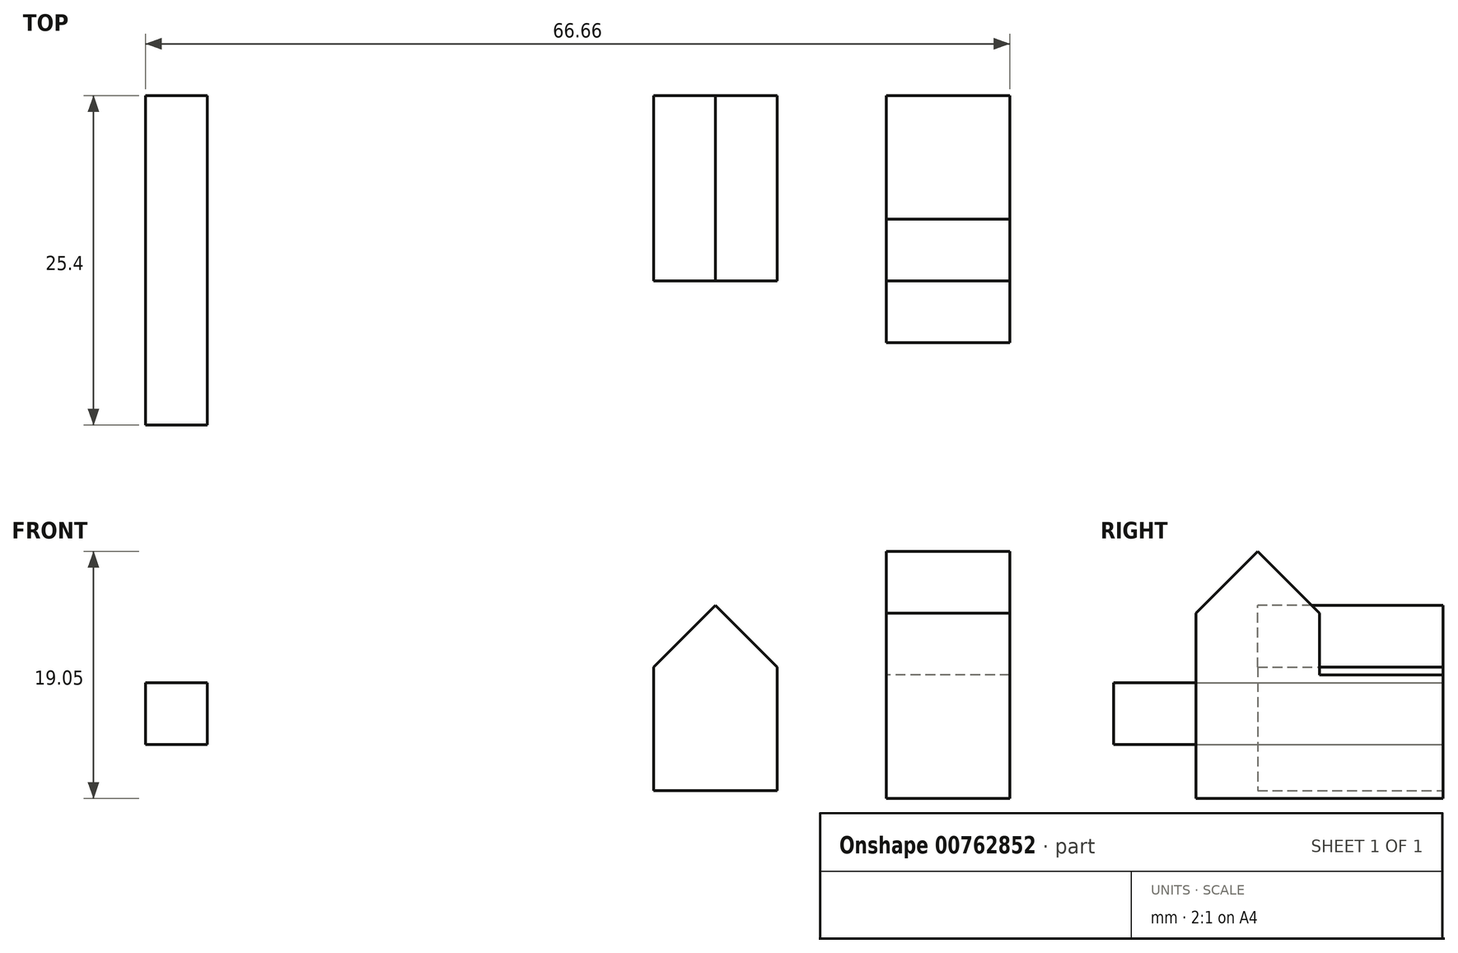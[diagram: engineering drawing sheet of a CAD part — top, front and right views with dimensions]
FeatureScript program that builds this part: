
annotation { "Feature Type Name" : "Feature", "Feature Type Description" : "" }
export const myFeature = defineFeature(function(context is Context, id is Id, definition is map)
    precondition{}
    {
        {
            var Q0;
            Q0=qCreatedBy(makeId("Front.planeOp"),FACE);
            var sketch = newSketch(context, id + "F0", { "sketchPlane" : qUnion([Q0])});
            skLineSegment(sketch, "E0", {"start": v(-30.1, 8.14) * mm, "end": v(-25.33, 8.14) * mm});
            skLineSegment(sketch, "E1", {"start": v(-25.33, 8.14) * mm, "end": v(-25.33, 12.9) * mm});
            skLineSegment(sketch, "E2", {"start": v(-25.33, 12.9) * mm, "end": v(-30.1, 12.9) * mm});
            skLineSegment(sketch, "E3", {"start": v(-30.1, 12.9) * mm, "end": v(-30.1, 8.14) * mm});
            skSolve(sketch);
        }
        {
            var Q0;
            Q0=makeQuery(id+"F0.imprint","IMPRINT",FACE,{"disambiguationData":[TD([[makeQuery(id+"F0.imprint","IMPRINT",EDGE,{"derivedFrom":sQuery(id+"F0.wireOp",EDGE,"E0")}),1.0]])]});
            extrude(context, id + "F1", {"entities" : qUnion([Q0]), "depth" : 25.4 * mm, "offsetDistance" : 25.4 * mm});
        }
        {
            var Q0;
            Q0=qCreatedBy(makeId("Front.planeOp"),FACE);
            var sketch = newSketch(context, id + "F2", { "sketchPlane" : qUnion([Q0])});
            skLineSegment(sketch, "E4", {"start": v(9.1, 14.1) * mm, "end": v(9.1, 4.57) * mm});
            skLineSegment(sketch, "E5", {"start": v(9.1, 4.57) * mm, "end": v(18.63, 4.57) * mm});
            skLineSegment(sketch, "E6", {"start": v(18.63, 4.57) * mm, "end": v(18.63, 14.1) * mm});
            skLineSegment(sketch, "E7", {"start": v(18.63, 14.1) * mm, "end": v(9.1, 14.1) * mm});
            skSolve(sketch);
        }
        {
            var Q0;
            Q0=makeQuery(id+"F2.imprint","IMPRINT",FACE,{"disambiguationData":[TD([[makeQuery(id+"F2.imprint","IMPRINT",EDGE,{"derivedFrom":sQuery(id+"F2.wireOp",EDGE,"E4")}),1.0]])]});
            extrude(context, id + "F3", {"entities" : qUnion([Q0]), "depth" : 14.29 * mm, "offsetDistance" : 25.4 * mm});
        }
        {
            var Q0;
            Q0=makeQuery(id+"F3.opExtrude","CAP_FACE",FACE,{"disambiguationData":[OSD([sQuery(id+"F2.wireOp",EDGE,"E4"),sQuery(id+"F2.wireOp",EDGE,"E5"),sQuery(id+"F2.wireOp",EDGE,"E6"),sQuery(id+"F2.wireOp",EDGE,"E7")])],"isStart":false});
            var sketch = newSketch(context, id + "F4", { "sketchPlane" : qUnion([Q0])});
            skLineSegment(sketch, "E8", {"start": v(13.87, 18.86) * mm, "end": v(9.1, 14.1) * mm});
            skLineSegment(sketch, "E9", {"start": v(9.1, 14.1) * mm, "end": v(18.63, 14.1) * mm});
            skLineSegment(sketch, "E10", {"start": v(18.63, 14.1) * mm, "end": v(13.87, 18.86) * mm});
            skSolve(sketch);
        }
        {
            var Q0;
            Q0=makeQuery(id+"F4.imprint","IMPRINT",FACE,{"disambiguationData":[TD([[makeQuery(id+"F4.imprint","IMPRINT",EDGE,{"derivedFrom":sQuery(id+"F4.wireOp",EDGE,"E8")}),1.0]])]});
            extrude(context, id + "F5", {"entities" : qUnion([Q0]), "operationType" : NewBodyOperationType.ADD, "oppositeDirection" : true, "depth" : 14.29 * mm, "offsetDistance" : 25.4 * mm});
        }
        {
            var Q0;
            Q0=qCreatedBy(makeId("Front.planeOp"),FACE);
            var sketch = newSketch(context, id + "F6", { "sketchPlane" : qUnion([Q0])});
            skLineSegment(sketch, "E11", {"start": v(27.04, 3.98) * mm, "end": v(36.56, 3.98) * mm});
            skLineSegment(sketch, "E12", {"start": v(36.56, 3.98) * mm, "end": v(36.56, 13.5) * mm});
            skLineSegment(sketch, "E13", {"start": v(36.56, 13.5) * mm, "end": v(27.04, 13.5) * mm});
            skLineSegment(sketch, "E14", {"start": v(27.04, 13.5) * mm, "end": v(27.04, 3.98) * mm});
            skSolve(sketch);
        }
        {
            var Q0;
            Q0=makeQuery(id+"F6.imprint","IMPRINT",FACE,{"disambiguationData":[TD([[makeQuery(id+"F6.imprint","IMPRINT",EDGE,{"derivedFrom":sQuery(id+"F6.wireOp",EDGE,"E11")}),1.0]])]});
            extrude(context, id + "F7", {"entities" : qUnion([Q0]), "depth" : 19.05 * mm, "offsetDistance" : 25.4 * mm});
        }
        {
            var Q0;
            Q0=makeQuery(id+"F7.opExtrude","CAP_FACE",FACE,{"disambiguationData":[OSD([sQuery(id+"F6.wireOp",EDGE,"E11"),sQuery(id+"F6.wireOp",EDGE,"E12"),sQuery(id+"F6.wireOp",EDGE,"E13"),sQuery(id+"F6.wireOp",EDGE,"E14")])],"isStart":false});
            var sketch = newSketch(context, id + "F8", { "sketchPlane" : qUnion([Q0])});
            skLineSegment(sketch, "E15", {"start": v(27.04, 13.5) * mm, "end": v(36.56, 13.5) * mm});
            skLineSegment(sketch, "E16", {"start": v(36.56, 13.5) * mm, "end": v(36.56, 18.26) * mm});
            skLineSegment(sketch, "E17", {"start": v(36.56, 18.26) * mm, "end": v(27.04, 18.26) * mm});
            skLineSegment(sketch, "E18", {"start": v(27.04, 18.26) * mm, "end": v(27.04, 13.5) * mm});
            skSolve(sketch);
        }
        {
            var Q0;
            Q0=makeQuery(id+"F8.imprint","IMPRINT",FACE,{"disambiguationData":[TD([[makeQuery(id+"F8.imprint","IMPRINT",EDGE,{"derivedFrom":sQuery(id+"F8.wireOp",EDGE,"E15")}),-1.0]])]});
            extrude(context, id + "F9", {"entities" : qUnion([Q0]), "operationType" : NewBodyOperationType.ADD, "oppositeDirection" : true, "depth" : 9.52 * mm, "offsetDistance" : 25.4 * mm});
        }
        {
            var Q0;
            Q0=makeQuery(id+"F9.boolean.opBoolean","MERGE",FACE,{"derivedFrom":[makeQuery(id+"F7.opExtrude","SWEPT_FACE",FACE,{"disambiguationData":[OSD([sQuery(id+"F6.wireOp",EDGE,"E12")])]}),makeQuery(id+"F9.opExtrude","SWEPT_FACE",FACE,{"disambiguationData":[OSD([sQuery(id+"F8.wireOp",EDGE,"E16")])]})]});
            var sketch = newSketch(context, id + "F10", { "sketchPlane" : qUnion([Q0])});
            skLineSegment(sketch, "E19", {"start": v(-14.29, 23.03) * mm, "end": v(-19.05, 18.26) * mm});
            skLineSegment(sketch, "E20", {"start": v(-19.05, 18.26) * mm, "end": v(-9.53, 18.26) * mm});
            skLineSegment(sketch, "E21", {"start": v(-9.52, 18.26) * mm, "end": v(-14.29, 23.03) * mm});
            skSolve(sketch);
        }
        {
            var Q0;
            Q0=makeQuery(id+"F10.imprint","IMPRINT",FACE,{"disambiguationData":[TD([[makeQuery(id+"F10.imprint","IMPRINT",EDGE,{"derivedFrom":sQuery(id+"F10.wireOp",EDGE,"E19")}),1.0]])]});
            extrude(context, id + "F11", {"entities" : qUnion([Q0]), "operationType" : NewBodyOperationType.ADD, "oppositeDirection" : true, "depth" : 9.52 * mm, "offsetDistance" : 25.4 * mm});
        }
    });
